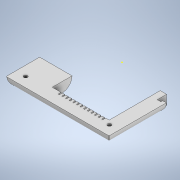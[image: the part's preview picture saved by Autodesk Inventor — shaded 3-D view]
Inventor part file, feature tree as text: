
AUTODESK INVENTOR PART (.ipt)
format: ipt  version: 2020 (Build 240168000, 168)  size: 1,033,216 bytes
history: native  units: mm
features: other x3, sketch x2, extrude x1
ambient origin geometry x8: Origin, YZ Plane, XZ Plane, XY Plane, X Axis, Y Axis, Z Axis, Center Point
bodies: Solid1 (feature_tree)
feature tree (6):
  other  "casing-backing.ipt"
  extrude  "Extrusion1"  Depth=10.0mm TaperAngle=0.0deg
  other  "Solid4::casing-backing.ipt"
  other  "TaggingFeature1"
  sketch  "Sketch1"  dims[d0=10.0mm d1=10.0mm d2=0.0mm]
  sketch  "Sketch6"  dims[d3=0.5mm d4=0.872665mm]
